# Revit family: NBS_Allermuir_OffcTbls_FortySeven_WorkLoungeTables
name_source: partatom
category: Furniture
revit_build: Autodesk Revit 2018 (Build: 20190510_1515(x64)
units: mm (PartAtom-declared; Revit-internal decimal feet)

## family parameters
Always vertical = Yes
Cut with Voids When Loaded = No
Room Calculation Point = No
Shared = No
Work Plane-Based = No

## types (2) — shared parameters
ABandLaminateRange = Formica - Fundamentals (Shell Finish), Polyrey - Durion
AssetType = Movable
BBandLaminateRange = Formica - Plain Colours, Formica - Patterns, Formica - Woods (matte 58), Formica - Fundamentals (All other Finishes)
CBandLaminateRange = Polyrey - Papago, Polyrey - Origine
Category = Pr_40_50_21_60:Office tables
Description = Work lounge square table
DurationUnit = year
EdgeProfile = 47
ExpectedLife = 10
Features = 25mm laminate faced MDF core top with a clear edge profile, Steel pedestal base finished in Black powder coat, Plastic glides with levelling adjustment, Table edge profile can be stained, Steel pedestal base available in White or Stone powder coat
Finish = Black, white, stone
IfcExportAs = IfcFurnitureType
IfcExportType = TABLE
IsBuiltIn = No
ManufacturerName = Allermuir
ManufacturerURL = www.allermuir.co.uk
Material = Plastic, Wood, Steel
ModelReference = FortySeven_WorkLoungeTables
NBSCertification = www.nationalbimlibrary.com/cert/kowj40mt
NBSDescription = Office tables
NBSReference = 45-35-20/340
NominalHeight = 640 mm  [stored 2.09974 ft]
ProductInformation = https://www.allermuir.com
Shape = Square
Status = UNSET
StockLaminateRange = White, Grey, Powder Blue, Sea Jade, Platinum, Pewter Grey, Jet Black, Ash, Summer Oak, Biella Walnut
Style = Table
SustainabilityPerformance = 13.50% recyclable
TableBaseMaterial = NBS_Allermuir_Steel_BlackPowderCoat
TableHeight = 640 mm  [stored 2.09974 ft]
TableTopMaterial = NBS_Allermuir_LaminateFacedMDF_Black
Uniclass2015Code = Pr_40_50_21_60
Uniclass2015Title = Office tables
Uniclass2015Version = Products v1.15
Version = 1
WarrantyDescription = Allermuir warrant that its manufactured products are free from manufacturing defects - in materials or workmanship - for a period of five (5) years. , Allermuir will repair, or replace (at Allermuir's sole discretion) with comparable free of charge materials / components, any product / component which fails under normal use in a single shift environment, as a result of a defect in the materials and/ or workmanship
WarrantyDurationParts = 5
WarrantyDurationUnit = year
zero-valued in all types: NumberOfChairs, WorksurfaceArea

## per-type parameters (varying)
| type | BIMObjectName | ModelNumber | Name | NominalDepth | NominalLength | NominalWidth | Size | TableTopCornerRadiusOffset | TableTopWidth |
| FortySeven_WorkLoungeTable_FRSW07SQ | NBS_Allermuir_OfficeTables_FortySeven_WorkLoungeTables_FRSW07SQ | FRSW07SQ | OfficeTables_FRSW07SQ_FortySeven_Allermuir | 750 mm  [stored 2.46063 ft] | 750 mm  [stored 2.46063 ft] | 750 mm  [stored 2.46063 ft] | 640 x 750 x 750 mm | 81 mm  [stored 0.265748 ft] | 750 mm  [stored 2.46063 ft] |
| FortySeven_WorkLoungeTable_FRSW09SQ | NBS_Allermuir_OfficeTables_FortySeven_WorkLoungeTables_FRSW09SQ | FRSW09SQ | OfficeTables_FRSW09SQ_FortySeven_Allermuir | 900 mm  [stored 2.95276 ft] | 900 mm  [stored 2.95276 ft] | 900 mm  [stored 2.95276 ft] | 640 x 900 x 900 mm | 84 mm  [stored 0.275591 ft] | 900 mm  [stored 2.95276 ft] |

note: [stored X ft] marks values corroborated as IEEE doubles in the binary element streams (Revit-internal decimal feet)

## geometry (parser evidence)
native form markers: Sweep x2
no freeform markers — native parametric forms only
